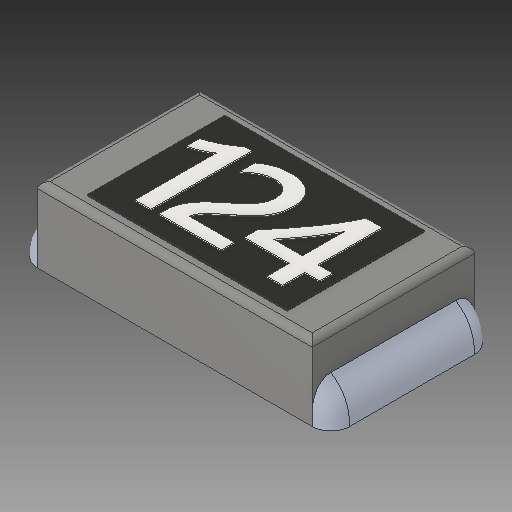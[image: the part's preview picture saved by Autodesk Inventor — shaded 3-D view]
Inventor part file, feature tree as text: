
AUTODESK INVENTOR PART (.ipt)
format: ipt  version: 2018.3 (Build 223284000, 284)  size: 227,840 bytes
history: native  units: mm
features: other x4, fillet x1, mirror x1
ambient origin geometry x8: Origin, YZ Plane, XZ Plane, XY Plane, X Axis, Y Axis, Z Axis, Center Point
bodies: Body1 (feature_tree), Body2 (feature_tree), Body3 (feature_tree)
feature tree (6):
  other  "Sólido1"
  other  "Sólido2"
  other  "Sólido3"
  fillet  "Fillet2"  [1 undecoded]
  mirror  "Mirror1"
  other  "Boss-Extrude4"
note: 1 required parameter value undecoded (feature->parameter linkage not recoverable at this tier; creation-order binding heuristic only, values carry confidence <= 0.55)
